# Revit family: LAMP_HANCE 48V 1000-2000 SUPER SPOT
name_source: partatom
category: Luminarias
revit_build: Autodesk Revit 2015 (Build: 20140606_1530(x64)
units: mm (PartAtom-declared; Revit-internal decimal feet)

## types (12) — shared parameters
CRI = 80
Comentarios de tipo = Availability of tilting between 0º and 90º, rotation between 0º and 355º and change ring color when placed in a project.
Diameter = 65 mm  [stored 0.213255 ft]
Elevación por defecto = 1219 mm
Fabricante = LAMP
Gear = Electronic
Height = 135 mm  [stored 0.442913 ft]
Installation instructions = https://www.lamp.es
Insulation class = III
Lamp = HIGH POWER LED
Last update = 27/03/2019
Luminaire type = Indoor - Spotlight
MacAdam = 3
Manufacturer URL = http://www.lamp.es
Manufacturer country = Spain
Manufacturer name = LAMP
Model explanation = Availability of tilting between 0º and 90º, rotation between 0º and 355º and change ring color when placed in a project.
Power Supply = 48V DC
Product URL = https://www.lamp.es
Product datasheet = http://www.lamp.es
Protection rating = IP20
Type = HIGH POWER CREE
Weight = 0.46 kg

## per-type parameters (varying)
| type | Descripción | Efficacy | Finish | IEE | Initial color | Initial intensity | LED Lifetime | Material tija | Modelo | Photometric web file | Plum | Power | Product code |
| 498LM 2700 SUPER SPOT BLACK | HANCE TRACK 48 1000 VWW SSP BK. | 53 lm/W | RAL9011 textured | A+ | 2700 K | 498 lm | 50.000 L90 | LAMP_Aluminio Hance Negro | HS1TL10SS827NBB | Cuerpo Hance 48V BASE 1000_2000 (tilting)_SS : 498LM 2700 SUPER SPOT BLACK | 9 W | 8 W | HS1TL10SS827NBB |
| 498LM 2700 SUPER SPOT WHITE | HANCE TRACK 48 1000 VWW SSP WH. | 53 lm/W | RAL9010 textured | A+ | 2700 K | 498 lm | 50.000 L90 | LAMP_Aluminio Hance Blanco | HS1TL10SS827NBW | Cuerpo Hance 48V BASE 1000_2000 (tilting)_SS : 498LM 2700 SUPER SPOT WHITE | 9 W | 8 W | HS1TL10SS827NBW |
| 498LM 3000 SUPER SPOT BLACK | HANCE TRACK 48 1000 WW SSP BK. | 53 lm/W | RAL9011 textured | A+ | 3000 K | 498 lm | 50.000 L90 | LAMP_Aluminio Hance Negro | HS1TL10SS830NBB | Cuerpo Hance 48V BASE 1000_2000 (tilting)_SS : 498LM 3000 SUPER SPOT BLACK | 9 W | 8 W | HS1TL10SS830NBB |
| 498LM 3000 SUPER SPOT WHITE | HANCE TRACK 48 1000 WW SSP WH. | 53 lm/W | RAL9010 textured | A+ | 3000 K | 498 lm | 50.000 L90 | LAMP_Aluminio Imag Blanco | HS1TL10SS830NBW | Cuerpo Hance 48V BASE 1000_2000 (tilting)_SS : 498LM 3000 SUPER SPOT WHITE | 9 W | 8 W | HS1TL10SS830NBW |
| 537LM 4000 SUPER SPOT BLACK | HANCE TRACK 48 1000 NW SSP BK. | 59 lm/W | RAL9011 textured | A+ | 4000 K | 537 lm | 50.000 L90 | LAMP_Aluminio Hance Negro | HS1TL10SS840NBB | Cuerpo Hance 48V BASE 1000_2000 (tilting)_SS : 537LM 4000 SUPER SPOT BLACK | 9 W | 8 W | HS1TL10SS840NBB |
| 537LM 4000 SUPER SPOT WHITE | HANCE TRACK 48 1000 NW SSP WH. | 59 lm/W | RAL9010 textured | A+ | 4000 K | 537 lm | 50.000 L90 | LAMP_Aluminio Hance Blanco | HS1TL10SS840NBW | Cuerpo Hance 48V BASE 1000_2000 (tilting)_SS : 537LM 4000 SUPER SPOT WHITE | 9 W | 8 W | HS1TL10SS840NBW |
| 689LM 2700 SUPER SPOT BLACK | HANCE TRACK 48 2000 VWW SSP BK. | 51 lm/W | RAL9011 textured | A | 2700 K | 689 lm | 50.000 L80 | LAMP_Aluminio Hance Negro | HS1TL20SS827NBB | Cuerpo Hance 48V BASE 1000_2000 (tilting)_SS : 689LM 2700 SUPER SPOT BLACK | 14 W | 12 W | HS1TL20SS827NBB |
| 689LM 2700 SUPER SPOT WHITE | HANCE TRACK 48 2000 VWW SSP WH. | 51 lm/W | RAL9010 textured | A | 2700 K | 689 lm | 50.000 L80 | LAMP_Aluminio Hance Blanco | HS1TL20SS827NBW | Cuerpo Hance 48V BASE 1000_2000 (tilting)_SS : 689LM 2700 SUPER SPOT WHITE | 14 W | 12 W | HS1TL20SS827NBW |
| 689LM 3000 SUPER SPOT BLACK | HANCE TRACK 48 2000 WW SSP BK. | 51 lm/W | RAL9011 textured | A | 3000 K | 689 lm | 50.000 L80 | LAMP_Aluminio Hance Negro | HS1TL20SS830NBB | Cuerpo Hance 48V BASE 1000_2000 (tilting)_SS : 689LM 3000 SUPER SPOT BLACK | 14 W | 12 W | HS1TL20SS830NBB |
| 689LM 3000 SUPER SPOT WHITE | HANCE TRACK 48 2000 WW SSP WH. | 51 lm/W | RAL9010 textured | A | 3000 K | 689 lm | 50.000 L80 | LAMP_Aluminio Hance Blanco | HS1TL20SS830NBW | Cuerpo Hance 48V BASE 1000_2000 (tilting)_SS : 689LM 3000 SUPER SPOT WHITE | 14 W | 12 W | HS1TL20SS830NBW |
| 746LM 4000 SUPER SPOT BLACK | HANCE TRACK 48 2000 NW SSP BK. | 55 lm/W | RAL9011 textured | A | 4000 K | 746 lm | 50.000 L80 | LAMP_Aluminio Hance Negro | HS1TL20SS840NBB | Cuerpo Hance 48V BASE 1000_2000 (tilting)_SS : 746LM 4000 SUPER SPOT BLACK | 14 W | 12 W | HS1TL20SS840NBB |
| 746LM 4000 SUPER SPOT WHITE | HANCE TRACK 48 2000 NW SSP WH. | 55 lm/W | RAL9010 textured | A | 4000 K | 746 lm | 50.000 L80 | LAMP_Aluminio Hance Blanco | HS1TL20SS840NBW | Cuerpo Hance 48V BASE 1000_2000 (tilting)_SS : 746LM 4000 SUPER SPOT WHITE | 14 W | 12 W | HS1TL20SS840NBW |

note: [stored X ft] marks values corroborated as IEEE doubles in the binary element streams (Revit-internal decimal feet)
